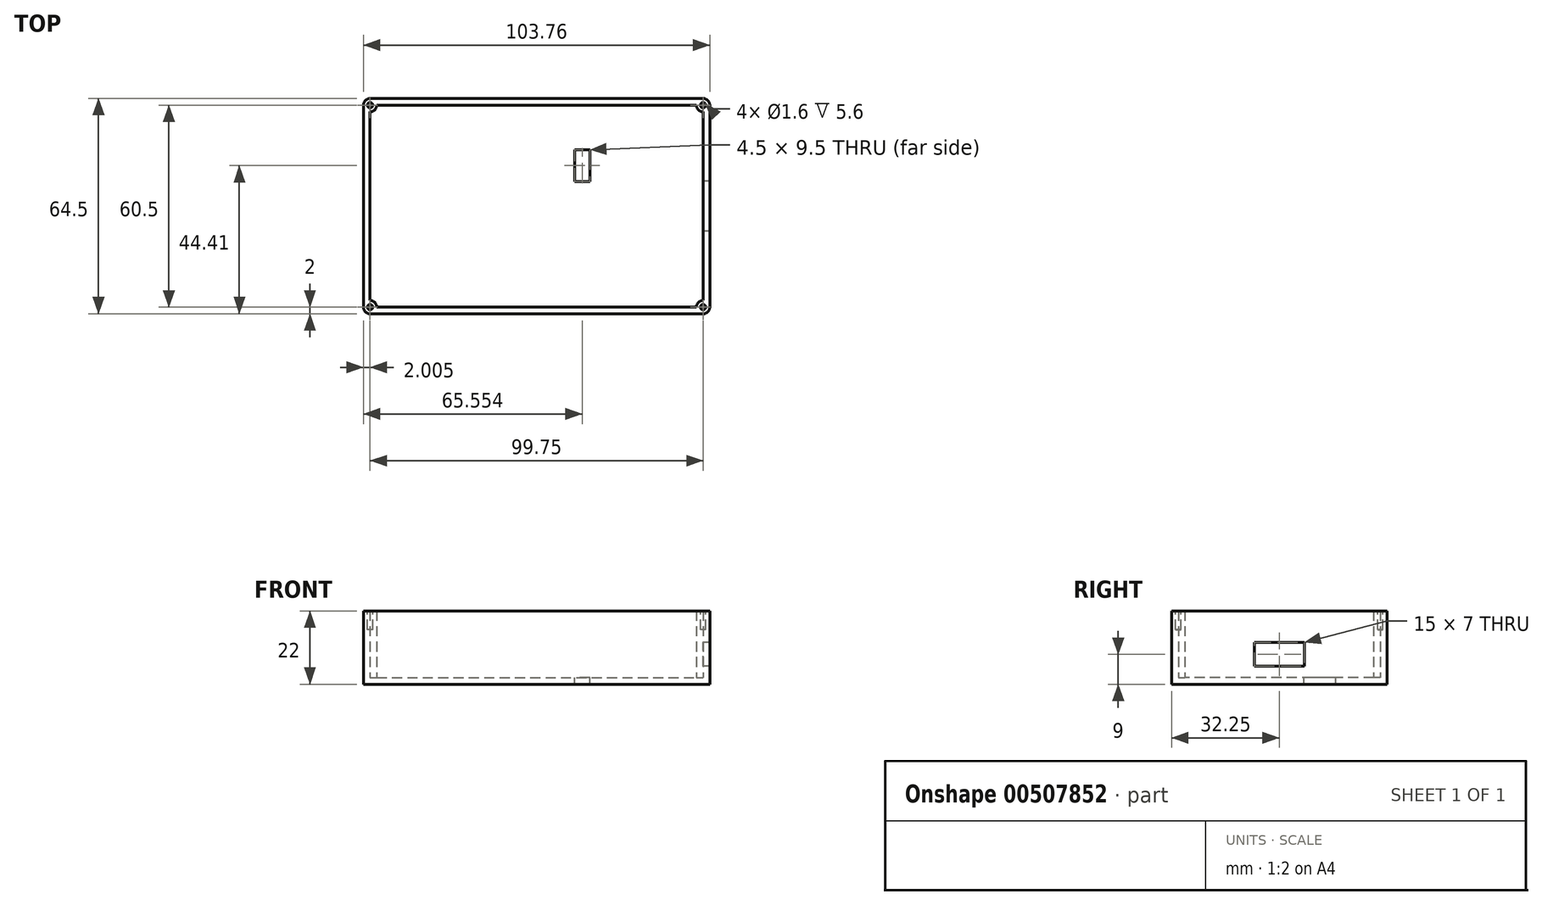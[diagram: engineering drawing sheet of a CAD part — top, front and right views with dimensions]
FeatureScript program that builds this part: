
annotation { "Feature Type Name" : "Feature", "Feature Type Description" : "" }
export const myFeature = defineFeature(function(context is Context, id is Id, definition is map)
    precondition{}
    {
        {
            var Q0;
            Q0=qCreatedBy(makeId("Top.planeOp"),FACE);
            var sketch = newSketch(context, id + "F0", { "sketchPlane" : qUnion([Q0])});
            skLineSegment(sketch, "E0.bottom", {"start": v(-51.88, 32.25) * mm, "end": v(51.88, 32.25) * mm});
            skLineSegment(sketch, "E0.top", {"start": v(-51.88, -32.25) * mm, "end": v(51.88, -32.25) * mm});
            skLineSegment(sketch, "E0.left", {"start": v(-51.88, 32.25) * mm, "end": v(-51.88, -32.25) * mm});
            skLineSegment(sketch, "E0.right", {"start": v(51.88, 32.25) * mm, "end": v(51.88, -32.25) * mm});
            skPoint(sketch, "E0.middle", {"position": v(0, 0) * mm});
            skPoint(sketch, "E1", {"position": v(-51.88, 0) * mm});
            skSolve(sketch);
        }
        {
            var Q0;
            Q0=makeQuery(id+"F0.imprint","IMPRINT",FACE,{"disambiguationData":[TD([[makeQuery(id+"F0.imprint","IMPRINT",EDGE,{"derivedFrom":sQuery(id+"F0.wireOp",EDGE,"E0.bottom")}),-1.0]])]});
            extrude(context, id + "F1", {"entities" : qUnion([Q0]), "depth" : 22 * mm});
        }
        {
            var Q0;
            Q0=makeQuery(id+"F1.opExtrude","CAP_FACE",FACE,{"disambiguationData":[OSD([sQuery(id+"F0.wireOp",EDGE,"E0.bottom"),sQuery(id+"F0.wireOp",EDGE,"E0.top"),sQuery(id+"F0.wireOp",EDGE,"E0.left"),sQuery(id+"F0.wireOp",EDGE,"E0.right")])],"isStart":false});
            shell(context, id + "F2", {"entities" : qUnion([Q0]), "thickness" : 2 * mm});
        }
        {
            var Q0;
            Q0=qCreatedBy(makeId("Right.planeOp"),FACE);
            var sketch = newSketch(context, id + "F3", { "sketchPlane" : qUnion([Q0])});
            skLineSegment(sketch, "E2.bottom", {"start": v(7.5, 12.5) * mm, "end": v(-7.5, 12.5) * mm});
            skLineSegment(sketch, "E2.top", {"start": v(7.5, 5.5) * mm, "end": v(-7.5, 5.5) * mm});
            skLineSegment(sketch, "E2.left", {"start": v(7.5, 12.5) * mm, "end": v(7.5, 5.5) * mm});
            skLineSegment(sketch, "E2.right", {"start": v(-7.5, 12.5) * mm, "end": v(-7.5, 5.5) * mm});
            skPoint(sketch, "E3", {"position": v(7.5, 9) * mm});
            skPoint(sketch, "E4", {"position": v(0, 5.5) * mm});
            skSolve(sketch);
        }
        {
            var Q0;
            Q0=qSketchRegion(id+"F3",true);
            extrude(context, id + "F4", {"entities" : qUnion([Q0]), "operationType" : NewBodyOperationType.REMOVE, "depth" : 381 * mm});
        }
        {
            var Q0;
            Q0=makeQuery(id+"F1.opExtrude","SWEPT_EDGE",EDGE,{"disambiguationData":[OSD([sQuery(id+"F0.wireOp",EDGE,"E0.bottom"),sQuery(id+"F0.wireOp",EDGE,"E0.left")])]});
            var Q1;
            Q1=makeQuery(id+"F1.opExtrude","SWEPT_EDGE",EDGE,{"disambiguationData":[OSD([sQuery(id+"F0.wireOp",EDGE,"E0.top"),sQuery(id+"F0.wireOp",EDGE,"E0.left")])]});
            var Q2;
            Q2=makeQuery(id+"F1.opExtrude","SWEPT_EDGE",EDGE,{"disambiguationData":[OSD([sQuery(id+"F0.wireOp",EDGE,"E0.top"),sQuery(id+"F0.wireOp",EDGE,"E0.right")])]});
            var Q3;
            Q3=makeQuery(id+"F1.opExtrude","SWEPT_EDGE",EDGE,{"disambiguationData":[OSD([sQuery(id+"F0.wireOp",EDGE,"E0.bottom"),sQuery(id+"F0.wireOp",EDGE,"E0.right")])]});
            fillet(context, id + "F5", {"entities" : qUnion([Q0, Q1, Q2, Q3]), "radius" : 2 * mm, "tangentPropagation" : true, "allowEdgeOverflow" : false});
        }
        {
            var Q0;
            Q0=qCreatedBy(makeId("Top.planeOp"),FACE);
            var sketch = newSketch(context, id + "F6", { "sketchPlane" : qUnion([Q0])});
            skPoint(sketch, "E5", {"position": v(-49.87, 0) * mm});
            skLineSegment(sketch, "E6.bottom", {"start": v(15.92, 16.9) * mm, "end": v(11.42, 16.9) * mm});
            skLineSegment(sketch, "E6.top", {"start": v(15.92, 7.4) * mm, "end": v(11.42, 7.4) * mm});
            skLineSegment(sketch, "E6.left", {"start": v(15.92, 16.9) * mm, "end": v(15.92, 7.4) * mm});
            skLineSegment(sketch, "E6.right", {"start": v(11.42, 16.9) * mm, "end": v(11.42, 7.4) * mm});
            skSolve(sketch);
        }
        {
            var Q0;
            Q0=qSketchRegion(id+"F6",true);
            extrude(context, id + "F7", {"entities" : qUnion([Q0]), "operationType" : NewBodyOperationType.REMOVE, "endBound" : BoundingType.SYMMETRIC, "oppositeDirection" : true, "depth" : 25.4 * mm});
        }
        {
            var Q0;
            Q0=qCreatedBy(makeId("Top.planeOp"),FACE);
            var sketch = newSketch(context, id + "F8", { "sketchPlane" : qUnion([Q0])});
            skCircle(sketch, "E7", {"center": v(-49.87, 30.25) * mm, "radius": 2 * mm});
            skSolve(sketch);
        }
        {
            var Q0;
            Q0 = qSketchRegion(id + "F8", true);
            extrude(context, id + "F9", {"entities" : qUnion([Q0]), "operationType" : NewBodyOperationType.ADD, "depth" : 22 * mm});
        }
        {
            var Q0;
            Q0=makeQuery(id+"F2.opShell","OFFSET_FACE",FACE,{"disambiguationData":[OSD([sQuery(id+"F0.wireOp",EDGE,"E0.bottom"),sQuery(id+"F0.wireOp",EDGE,"E0.top"),sQuery(id+"F0.wireOp",EDGE,"E0.left"),sQuery(id+"F0.wireOp",EDGE,"E0.right")])]});
            var sketch = newSketch(context, id + "F10", { "sketchPlane" : qUnion([Q0])});
            skCircle(sketch, "E8", {"center": v(-49.88, -30.25) * mm, "radius": 2 * mm});
            skSolve(sketch);
        }
        {
            var Q0;
            Q0 = qSketchRegion(id + "F10", true);
            extrude(context, id + "F11", {"entities" : qUnion([Q0]), "operationType" : NewBodyOperationType.ADD, "depth" : 20 * mm});
        }
        {
            var Q0;
            Q0=makeQuery(id+"F2.opShell","OFFSET_FACE",FACE,{"disambiguationData":[OSD([sQuery(id+"F0.wireOp",EDGE,"E0.bottom"),sQuery(id+"F0.wireOp",EDGE,"E0.top"),sQuery(id+"F0.wireOp",EDGE,"E0.left"),sQuery(id+"F0.wireOp",EDGE,"E0.right")])]});
            var sketch = newSketch(context, id + "F12", { "sketchPlane" : qUnion([Q0])});
            skCircle(sketch, "E9", {"center": v(49.88, -30.25) * mm, "radius": 2 * mm});
            skSolve(sketch);
        }
        {
            var Q0;
            Q0 = qSketchRegion(id + "F12", true);
            extrude(context, id + "F13", {"entities" : qUnion([Q0]), "operationType" : NewBodyOperationType.ADD, "depth" : 20 * mm});
        }
        {
            var Q0;
            Q0=qCreatedBy(makeId("Top.planeOp"),FACE);
            var sketch = newSketch(context, id + "F14", { "sketchPlane" : qUnion([Q0])});
            skCircle(sketch, "E10", {"center": v(49.88, 30.25) * mm, "radius": 2 * mm});
            skSolve(sketch);
        }
        {
            var Q0;
            Q0 = qSketchRegion(id + "F14", true);
            extrude(context, id + "F15", {"entities" : qUnion([Q0]), "operationType" : NewBodyOperationType.ADD, "depth" : 22 * mm});
        }
        {
            var Q0;
            Q0=makeQuery(id+"F15.boolean.opBoolean","MERGE",FACE,{"derivedFrom":[makeQuery(id+"F11.boolean.opBoolean","MERGE",FACE,{"derivedFrom":[makeQuery(id+"F9.boolean.opBoolean","MERGE",FACE,{"derivedFrom":[makeQuery(id+"F1.opExtrude","CAP_FACE",FACE,{"disambiguationData":[OSD([sQuery(id+"F0.wireOp",EDGE,"E0.bottom"),sQuery(id+"F0.wireOp",EDGE,"E0.top"),sQuery(id+"F0.wireOp",EDGE,"E0.left"),sQuery(id+"F0.wireOp",EDGE,"E0.right")])],"isStart":false}),makeQuery(id+"F9.opExtrude","CAP_FACE",FACE,{"disambiguationData":[OSD([sQuery(id+"F8.wireOp",EDGE,"E7")])],"isStart":false})]}),makeQuery(id+"F11.opExtrude","CAP_FACE",FACE,{"disambiguationData":[OSD([sQuery(id+"F10.wireOp",EDGE,"E8")])],"isStart":false})]}),makeQuery(id+"F15.opExtrude","CAP_FACE",FACE,{"disambiguationData":[OSD([sQuery(id+"F14.wireOp",EDGE,"E10")])],"isStart":false})]});
            var sketch = newSketch(context, id + "F16", { "sketchPlane" : qUnion([Q0])});
            skCircle(sketch, "E11", {"center": v(-49.88, 30.25) * mm, "radius": 0.8 * mm});
            skSolve(sketch);
        }
        {
            var Q0;
            Q0 = qSketchRegion(id + "F16", true);
            extrude(context, id + "F17", {"entities" : qUnion([Q0]), "operationType" : NewBodyOperationType.REMOVE, "oppositeDirection" : true, "depth" : 5.6 * mm});
        }
        {
            var Q0;
            Q0=makeQuery(id+"F15.boolean.opBoolean","MERGE",FACE,{"derivedFrom":[makeQuery(id+"F13.boolean.opBoolean","MERGE",FACE,{"derivedFrom":[makeQuery(id+"F11.boolean.opBoolean","MERGE",FACE,{"derivedFrom":[makeQuery(id+"F9.boolean.opBoolean","MERGE",FACE,{"derivedFrom":[makeQuery(id+"F1.opExtrude","CAP_FACE",FACE,{"disambiguationData":[OSD([sQuery(id+"F0.wireOp",EDGE,"E0.bottom"),sQuery(id+"F0.wireOp",EDGE,"E0.top"),sQuery(id+"F0.wireOp",EDGE,"E0.left"),sQuery(id+"F0.wireOp",EDGE,"E0.right")])],"isStart":false}),makeQuery(id+"F9.opExtrude","CAP_FACE",FACE,{"disambiguationData":[OSD([sQuery(id+"F8.wireOp",EDGE,"E7")])],"isStart":false})]}),makeQuery(id+"F11.opExtrude","CAP_FACE",FACE,{"disambiguationData":[OSD([sQuery(id+"F10.wireOp",EDGE,"E8")])],"isStart":false})]}),makeQuery(id+"F13.opExtrude","CAP_FACE",FACE,{"disambiguationData":[OSD([sQuery(id+"F12.wireOp",EDGE,"E9")])],"isStart":false})]}),makeQuery(id+"F15.opExtrude","CAP_FACE",FACE,{"disambiguationData":[OSD([sQuery(id+"F14.wireOp",EDGE,"E10")])],"isStart":false})]});
            var sketch = newSketch(context, id + "F18", { "sketchPlane" : qUnion([Q0])});
            skCircle(sketch, "E12", {"center": v(-49.88, -30.25) * mm, "radius": 0.8 * mm});
            skSolve(sketch);
        }
        {
            var Q0;
            Q0 = qSketchRegion(id + "F18", true);
            extrude(context, id + "F19", {"entities" : qUnion([Q0]), "operationType" : NewBodyOperationType.REMOVE, "oppositeDirection" : true, "depth" : 5.6 * mm});
        }
        {
            var Q0;
            Q0=makeQuery(id+"F15.boolean.opBoolean","MERGE",FACE,{"derivedFrom":[makeQuery(id+"F13.boolean.opBoolean","MERGE",FACE,{"derivedFrom":[makeQuery(id+"F11.boolean.opBoolean","MERGE",FACE,{"derivedFrom":[makeQuery(id+"F9.boolean.opBoolean","MERGE",FACE,{"derivedFrom":[makeQuery(id+"F1.opExtrude","CAP_FACE",FACE,{"disambiguationData":[OSD([sQuery(id+"F0.wireOp",EDGE,"E0.bottom"),sQuery(id+"F0.wireOp",EDGE,"E0.top"),sQuery(id+"F0.wireOp",EDGE,"E0.left"),sQuery(id+"F0.wireOp",EDGE,"E0.right")])],"isStart":false}),makeQuery(id+"F9.opExtrude","CAP_FACE",FACE,{"disambiguationData":[OSD([sQuery(id+"F8.wireOp",EDGE,"E7")])],"isStart":false})]}),makeQuery(id+"F11.opExtrude","CAP_FACE",FACE,{"disambiguationData":[OSD([sQuery(id+"F10.wireOp",EDGE,"E8")])],"isStart":false})]}),makeQuery(id+"F13.opExtrude","CAP_FACE",FACE,{"disambiguationData":[OSD([sQuery(id+"F12.wireOp",EDGE,"E9")])],"isStart":false})]}),makeQuery(id+"F15.opExtrude","CAP_FACE",FACE,{"disambiguationData":[OSD([sQuery(id+"F14.wireOp",EDGE,"E10")])],"isStart":false})]});
            var sketch = newSketch(context, id + "F20", { "sketchPlane" : qUnion([Q0])});
            skCircle(sketch, "E13", {"center": v(49.88, -30.25) * mm, "radius": 0.8 * mm});
            skSolve(sketch);
        }
        {
            var Q0;
            Q0 = qSketchRegion(id + "F20", true);
            extrude(context, id + "F21", {"entities" : qUnion([Q0]), "operationType" : NewBodyOperationType.REMOVE, "oppositeDirection" : true, "depth" : 5.6 * mm});
        }
        {
            var Q0;
            Q0=makeQuery(id+"F15.boolean.opBoolean","MERGE",FACE,{"derivedFrom":[makeQuery(id+"F13.boolean.opBoolean","MERGE",FACE,{"derivedFrom":[makeQuery(id+"F11.boolean.opBoolean","MERGE",FACE,{"derivedFrom":[makeQuery(id+"F9.boolean.opBoolean","MERGE",FACE,{"derivedFrom":[makeQuery(id+"F1.opExtrude","CAP_FACE",FACE,{"disambiguationData":[OSD([sQuery(id+"F0.wireOp",EDGE,"E0.bottom"),sQuery(id+"F0.wireOp",EDGE,"E0.top"),sQuery(id+"F0.wireOp",EDGE,"E0.left"),sQuery(id+"F0.wireOp",EDGE,"E0.right")])],"isStart":false}),makeQuery(id+"F9.opExtrude","CAP_FACE",FACE,{"disambiguationData":[OSD([sQuery(id+"F8.wireOp",EDGE,"E7")])],"isStart":false})]}),makeQuery(id+"F11.opExtrude","CAP_FACE",FACE,{"disambiguationData":[OSD([sQuery(id+"F10.wireOp",EDGE,"E8")])],"isStart":false})]}),makeQuery(id+"F13.opExtrude","CAP_FACE",FACE,{"disambiguationData":[OSD([sQuery(id+"F12.wireOp",EDGE,"E9")])],"isStart":false})]}),makeQuery(id+"F15.opExtrude","CAP_FACE",FACE,{"disambiguationData":[OSD([sQuery(id+"F14.wireOp",EDGE,"E10")])],"isStart":false})]});
            var sketch = newSketch(context, id + "F22", { "sketchPlane" : qUnion([Q0])});
            skCircle(sketch, "E14", {"center": v(49.88, 30.25) * mm, "radius": 0.8 * mm});
            skSolve(sketch);
        }
        {
            var Q0;
            Q0 = qSketchRegion(id + "F22", true);
            extrude(context, id + "F23", {"entities" : qUnion([Q0]), "operationType" : NewBodyOperationType.REMOVE, "oppositeDirection" : true, "depth" : 5.6 * mm});
        }
    });
